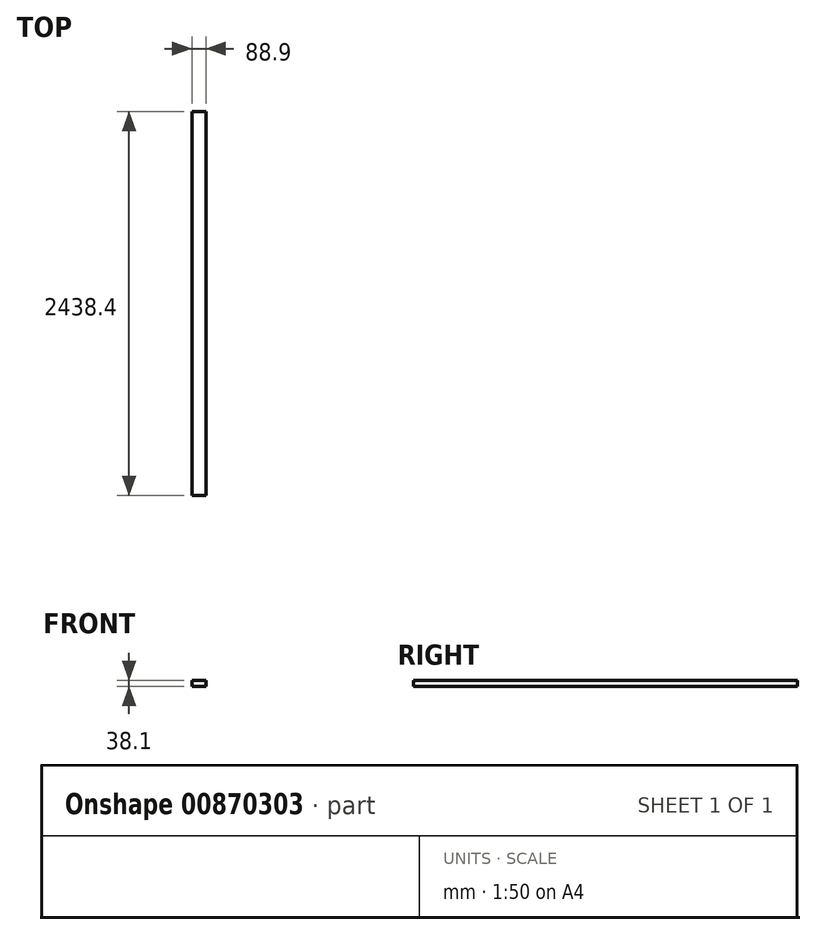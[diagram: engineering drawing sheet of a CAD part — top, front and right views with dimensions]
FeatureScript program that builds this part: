
annotation { "Feature Type Name" : "Feature", "Feature Type Description" : "" }
export const myFeature = defineFeature(function(context is Context, id is Id, definition is map)
    precondition{}
    {
        {
            var Q0;
            Q0=qCreatedBy(makeId("Front.planeOp"),FACE);
            var sketch = newSketch(context, id + "F0", { "sketchPlane" : qUnion([Q0])});
            skLineSegment(sketch, "E0.bottom", {"start": v(0, 0) * mm, "end": v(88.9, 0) * mm});
            skLineSegment(sketch, "E0.top", {"start": v(0, 38.1) * mm, "end": v(88.9, 38.1) * mm});
            skLineSegment(sketch, "E0.left", {"start": v(0, 0) * mm, "end": v(0, 38.1) * mm});
            skLineSegment(sketch, "E0.right", {"start": v(88.9, 0) * mm, "end": v(88.9, 38.1) * mm});
            skSolve(sketch);
        }
        {
            var Q0;
            Q0=makeQuery(id+"F0.imprint","IMPRINT",FACE,{"disambiguationData":[TD([[makeQuery(id+"F0.imprint","IMPRINT",EDGE,{"derivedFrom":sQuery(id+"F0.wireOp",EDGE,"E0.bottom")}),1.0]])]});
            extrude(context, id + "F1", {"entities" : qUnion([Q0]), "depth" : 2438.4 * mm, "offsetDistance" : 25.4 * mm});
        }
    });
